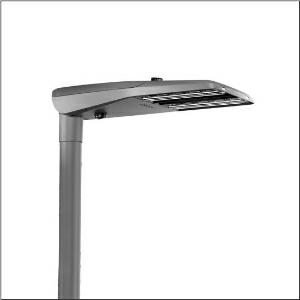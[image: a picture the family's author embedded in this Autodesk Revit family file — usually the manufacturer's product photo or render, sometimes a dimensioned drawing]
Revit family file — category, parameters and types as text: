
# Revit family: streetlight_sl_11_iq_midi___st1_2p1_0_5xc3g51y08me_d530
name_source: partatom
category: Lighting Fixtures
units: mm (PartAtom-declared; Revit-internal decimal feet)

## family parameters
Cut with Voids When Loaded = No
Host = Face
Light Source = No
Part Type = Normal
Room Calculation Point = No
Round Connector Dimension = Use Diameter
Shared = No

## types (1)
- --- (1 x LED, 17750 lm, 119.8 W, 3000K)
    Apparent Load = 120 VA
    CIE Flux Codes = 31 68 95 100 100
    Color Rendering = 70
    Color Temperature = 3000K
    Default Elevation = 1800 mm
    Description = Streetlight SL 11 iQ midi, mast luminaire, primary light control with 3 zone facetted reflector, of plastic, silver coated, highly specular, primary optical cover: cover, of PMMA, transparent, light distribution: ST1.2P1.0, light emission: direct distribution, primary light characteristic: asymmetric, installation type: post-top, side-entry, lamps: LED, High Power LED, rated values: 17.750lm | 119,8W | 148,2lm/W (begin service life); end service life: 17.750lm | 126,7W; at 50% lumin. flux: 8.875lm | 54,9W | 161,7lm/W, colour temperature: 3000K, colour rendering: CRI > 70, light colour: 730, light setting 1 begin service life: 100% | 17.750lm | 119,8W | 148,2lm/W | 3.000K, light setting 1 end service life: 126,7W, further light settings possible, control: pre-setting: logarithmic dimming characteristic, Street-Remote, Auto-Match, Temp-Guard, Lumen-Switch, Night-Set, Smart-Wire, Light-Fading, Desk-Remote (wireless, voltage-free reading and setting of iQ features in the workshop via application-optimized NFC function/RFID function), optimised constant luminous flux control (CLO 2.0), with cable H07RN-F 5x 1.5mm², mains connection: 230..240V, AC, 50/60Hz, connection cable pre-assembled, cable length: 12,5m, luminaire housing, of diecast aluminium, powder-coated, Siteco® metallic grey (DB 702S), please order mast flange separately, inclination adjustable without tools: 0°, 5°, 10°, 15° (post-top) | 0°, -5°, -10°, -15° (side-entry), sealing non-destructively replaceable, multi-level sealing system, length: 780mm, width: 376mm, height: 118mm, mast flange for spigot size: 42mm (side-entry): 5XC10008XM4, 60/48mm (side-entry/post-top): 5XC10108XM2, 76/60mm (side-entry/post-top): 5XC10108XM1, equipment: Power, Smart Interface below and above, protection rating (complete): IP66, insulation class (complete): insulation class II (safety insulation), certification: CE, ENEC, ENEC+, VDE, UKCA, impact resistance: IK10, permissible operating ambient temperature for outdoor applications: -25..+50°C, standard-compliant lighting for roads and squares, Environmental Product Declaration (EPD) tested and certified by an independent institute, packaging unit: 1 piece

Light Distribution: ST1.2P1.0
    Height = 118 mm
    Lamp = 1 x LED
    Lamp Light Flux = 17750 lm
    Lamp Power = 119.8 W
    Lamp count = 1
    Length = 780 mm
    Luminous efficacy = 148 lm/W
    Manufacturer = Siteco
    ModVariant = No
    Model = 5XC3G51Y08ME
    Number of Poles = 1
    OnlyDefault = Yes
    Power Factor = 1
    Product Name = Streetlight SL 11 iQ midi | ST1.2P1.0
    Product group = mast luminaire | pylon top
    ProductGroupID = 6100
    Protection Class = Protection class II
    Protection Degree = IP 66
    RLX_Detail_Level = 1
    RLX_Emergency_Light_Flux = 0 lm
    RLX_Emergency_Type = 0
    RLX_Emergency_Type_DB = No
    RlxData = <blob elided: 69913 chars, md5=15b0bd8a>
    Socket = socket
    Standby Power = 0 W
    System Light Flux = 17750 lm
    System Power = 120 W
    Type Comments = factory setting: luminous flux: 100 % | dim-lin: 254 | 540 mA
    Type Image = l_1004429.jpg
    URL = http://relux.com
    VarID = @adj_037048
    Voltage = 0 V
    Weight = 0.00 kg
    Width = 376 mm

## geometry (parser evidence)
native form markers: Blend x4, Sweep x10
no freeform markers — native parametric forms only
